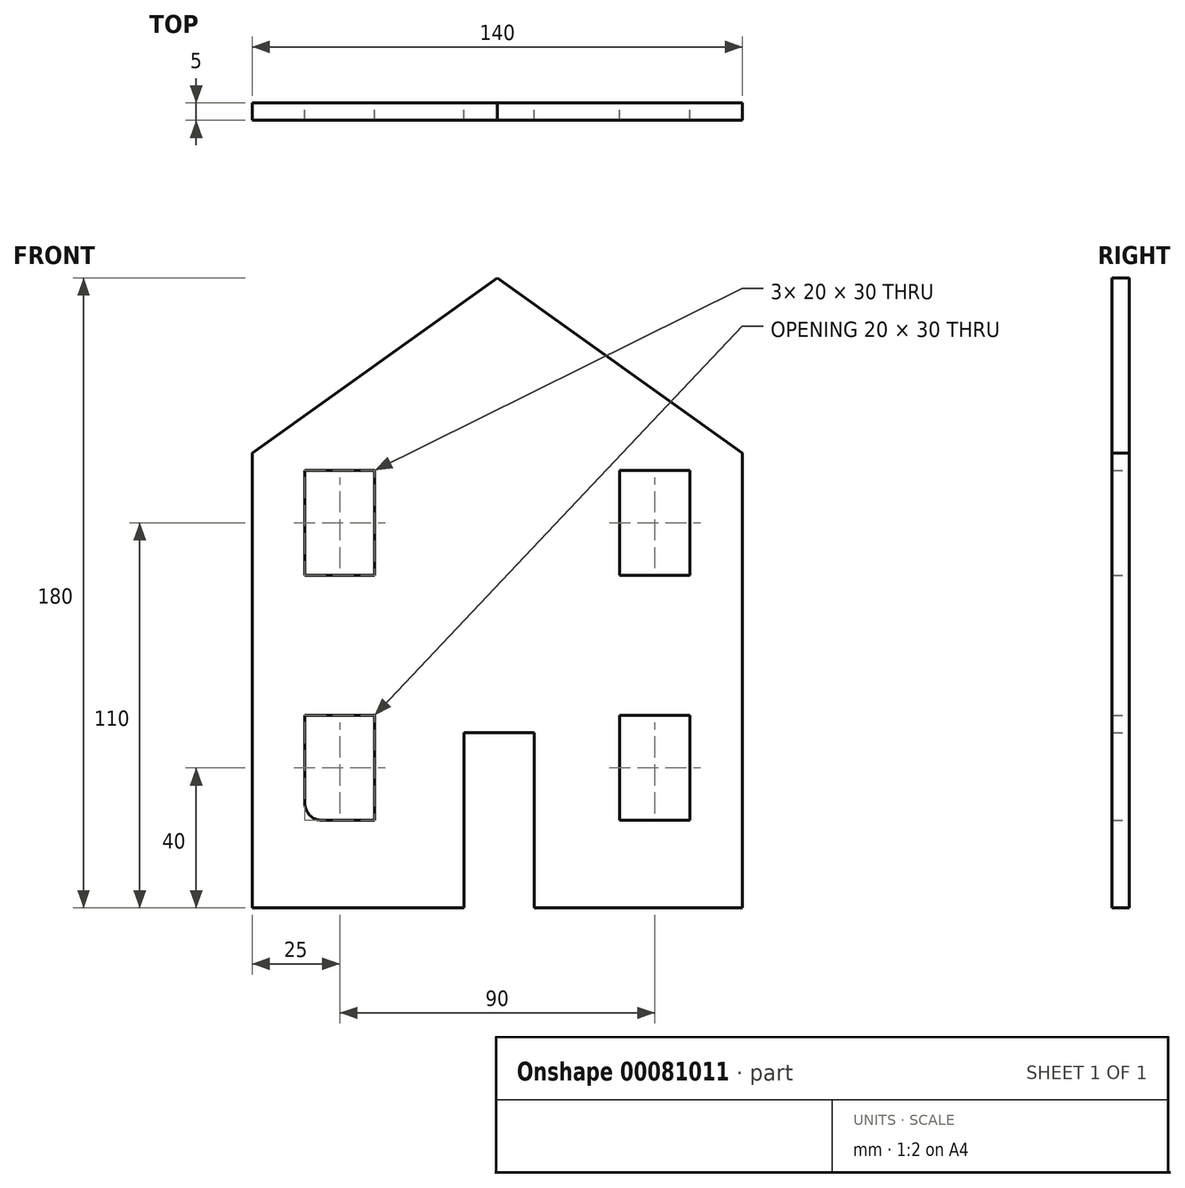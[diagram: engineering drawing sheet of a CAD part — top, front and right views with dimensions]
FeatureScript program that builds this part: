
annotation { "Feature Type Name" : "Feature", "Feature Type Description" : "" }
export const myFeature = defineFeature(function(context is Context, id is Id, definition is map)
    precondition{}
    {
        {
            var Q0;
            Q0=qCreatedBy(makeId("Front.planeOp"),FACE);
            var sketch = newSketch(context, id + "F0", { "sketchPlane" : qUnion([Q0])});
            skLineSegment(sketch, "E0.bottom", {"start": v(70, 0) * mm, "end": v(-70, 0) * mm});
            skLineSegment(sketch, "E0.left", {"start": v(70, 0) * mm, "end": v(70, 130) * mm});
            skLineSegment(sketch, "E1", {"start": v(0, 180) * mm, "end": v(70, 130) * mm});
            skLineSegment(sketch, "E2", {"start": v(-9.46, 0) * mm, "end": v(-9.46, 50) * mm});
            skLineSegment(sketch, "E3", {"start": v(-9.46, 50) * mm, "end": v(10.54, 50) * mm});
            skLineSegment(sketch, "E4", {"start": v(10.54, 50) * mm, "end": v(10.54, 0) * mm});
            skLineSegment(sketch, "E5", {"start": v(10.54, 0) * mm, "end": v(-9.46, 0) * mm});
            skLineSegment(sketch, "E6.bottom", {"start": v(-55, 55) * mm, "end": v(-35, 55) * mm});
            skLineSegment(sketch, "E6.top", {"start": v(-55, 25) * mm, "end": v(-35, 25) * mm});
            skLineSegment(sketch, "E6.left", {"start": v(-55, 55) * mm, "end": v(-55, 25) * mm});
            skLineSegment(sketch, "E6.right", {"start": v(-35, 55) * mm, "end": v(-35, 25) * mm});
            skLineSegment(sketch, "E7", {"start": v(-70, 80) * mm, "end": v(70, 80) * mm});
            skLineSegment(sketch, "E8", {"start": v(-55, 95) * mm, "end": v(-55, 125) * mm});
            skLineSegment(sketch, "E9", {"start": v(-55, 125) * mm, "end": v(-35, 125) * mm});
            skPoint(sketch, "E10", {"position": v(0, 0) * mm});
            skPoint(sketch, "E11", {"position": v(0, 130) * mm});
            skLineSegment(sketch, "E12", {"start": v(0, 130) * mm, "end": v(0, 0) * mm, "construction": true});
            skLineSegment(sketch, "E13", {"start": v(-55, 95) * mm, "end": v(-35, 95) * mm});
            skLineSegment(sketch, "E14", {"start": v(-35, 125) * mm, "end": v(-35, 95) * mm});
            skLineSegment(sketch, "E15.MirrorCS", {"start": v(35, 125) * mm, "end": v(35, 95) * mm});
            skLineSegment(sketch, "E16.MirrorCS", {"start": v(55, 95) * mm, "end": v(35, 95) * mm});
            skLineSegment(sketch, "E17.MirrorCS", {"start": v(55, 95) * mm, "end": v(55, 125) * mm});
            skLineSegment(sketch, "E18.MirrorCS", {"start": v(55, 125) * mm, "end": v(35, 125) * mm});
            skLineSegment(sketch, "E19.MirrorCS", {"start": v(35, 55) * mm, "end": v(35, 25) * mm});
            skLineSegment(sketch, "E20.MirrorCS", {"start": v(55, 55) * mm, "end": v(35, 55) * mm});
            skLineSegment(sketch, "E21.MirrorCS", {"start": v(55, 55) * mm, "end": v(55, 25) * mm});
            skLineSegment(sketch, "E22.MirrorCS", {"start": v(55, 25) * mm, "end": v(35, 25) * mm});
            skLineSegment(sketch, "E23", {"start": v(-70, 0) * mm, "end": v(-70, 80) * mm});
            skLineSegment(sketch, "E24", {"start": v(-70, 80) * mm, "end": v(-70, 130) * mm});
            skLineSegment(sketch, "E25", {"start": v(-70, 130) * mm, "end": v(0, 180) * mm});
            skLineSegment(sketch, "E26", {"start": v(-70, 130) * mm, "end": v(70, 130) * mm, "construction": true});
            skPoint(sketch, "E27", {"position": v(-24.41, 162.56) * mm});
            skLineSegment(sketch, "E28", {"start": v(0, 130) * mm, "end": v(0, 180) * mm, "construction": true});
            skPoint(sketch, "E29.MirrorP", {"position": v(24.41, 162.56) * mm});
            skSolve(sketch);
        }
        {
            var Q0;
            {var subQ1=sQuery(id+"F0.wireOp",EDGE,"E1");Q0=makeQuery(id+"F0.imprint","IMPRINT",FACE,{"disambiguationData":[TD([[makeQuery(id+"F0.imprint","IMPRINT",EDGE,{"derivedFrom":subQ1}),-1.0]])]});}
            var Q1;
            {var subQ6=sQuery(id+"F0.wireOp",EDGE,"E2");Q1=makeQuery(id+"F0.imprint","IMPRINT",FACE,{"disambiguationData":[TD([[makeQuery(id+"F0.imprint","IMPRINT",EDGE,{"derivedFrom":subQ6}),1.0]])]});}
            extrude(context, id + "F1", {"entities" : qUnion([Q0, Q1]), "endBound" : BoundingType.SYMMETRIC, "depth" : 5 * mm});
        }
        {
            var Q0;
            Q0=makeQuery(id+"F1.opExtrude","SWEPT_EDGE",EDGE,{"disambiguationData":[OSD([sQuery(id+"F0.wireOp",EDGE,"E6.top"),sQuery(id+"F0.wireOp",EDGE,"E6.left")])]});
            fillet(context, id + "F2", {"entities" : qUnion([Q0]), "radius" : 5 * mm, "tangentPropagation" : true, "allowEdgeOverflow" : false});
        }
    });
